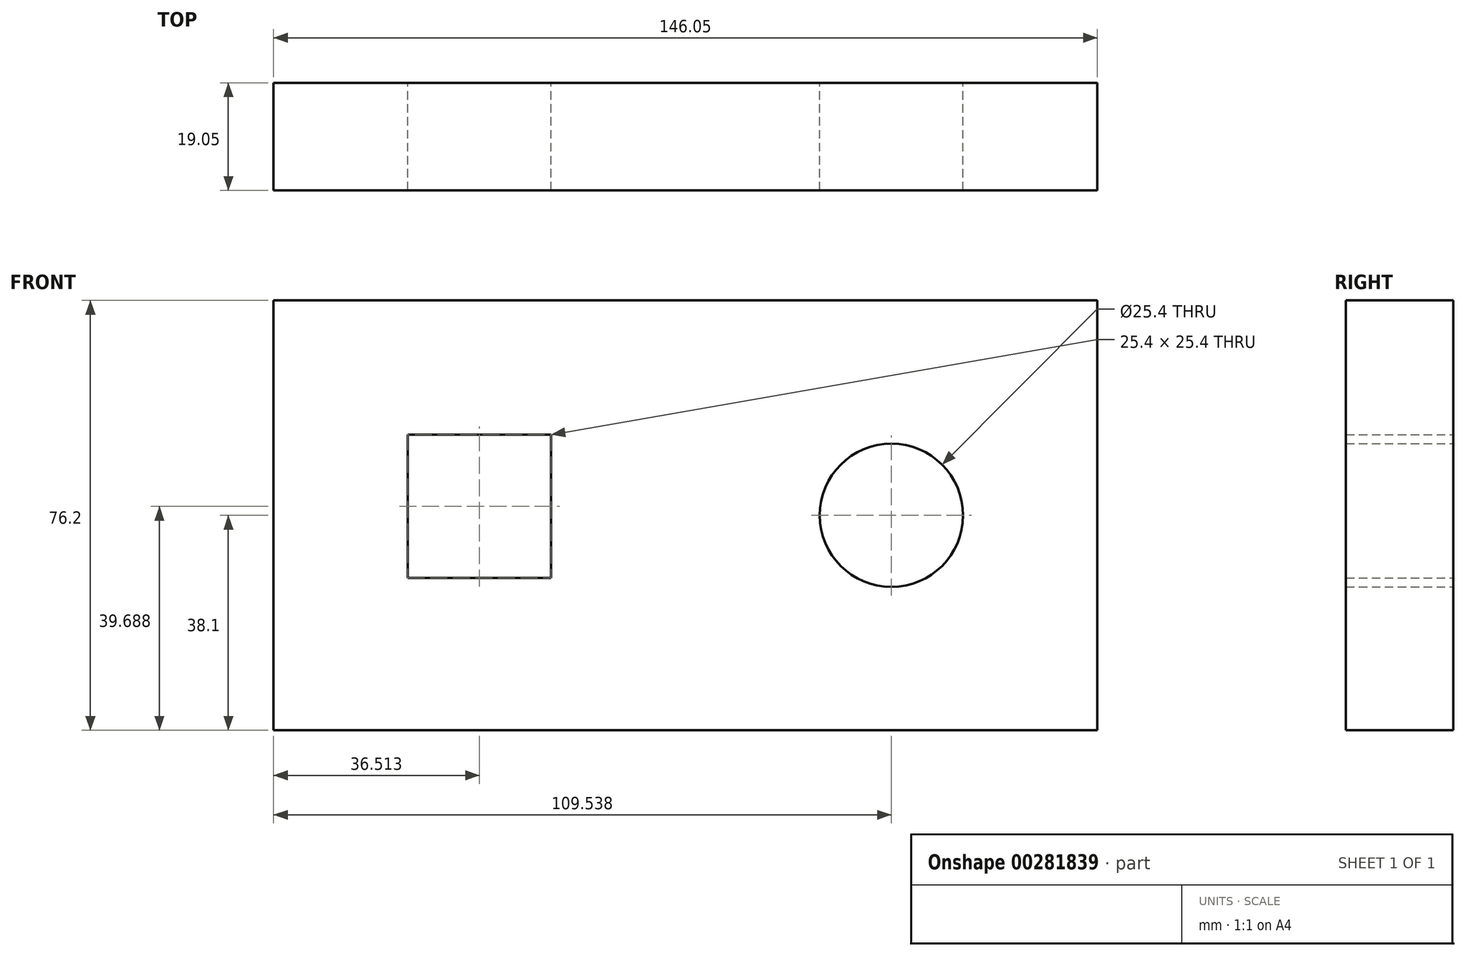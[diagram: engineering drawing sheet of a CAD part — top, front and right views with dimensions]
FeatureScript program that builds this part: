
annotation { "Feature Type Name" : "Feature", "Feature Type Description" : "" }
export const myFeature = defineFeature(function(context is Context, id is Id, definition is map)
    precondition{}
    {
        {
            var Q0;
            Q0=qCreatedBy(makeId("Front.planeOp"),FACE);
            var sketch = newSketch(context, id + "F0", { "sketchPlane" : qUnion([Q0])});
            skLineSegment(sketch, "E0.bottom", {"start": v(0, 0) * mm, "end": v(-146.05, 0) * mm});
            skLineSegment(sketch, "E0.top", {"start": v(0, 76.2) * mm, "end": v(-146.05, 76.2) * mm});
            skLineSegment(sketch, "E0.left", {"start": v(0, 0) * mm, "end": v(0, 76.2) * mm});
            skLineSegment(sketch, "E0.right", {"start": v(-146.05, 0) * mm, "end": v(-146.05, 76.2) * mm});
            skCircle(sketch, "E1", {"center": v(-36.51, 38.1) * mm, "radius": 12.7 * mm});
            skLineSegment(sketch, "E2.bottom", {"start": v(-122.24, 52.39) * mm, "end": v(-96.84, 52.39) * mm});
            skLineSegment(sketch, "E2.top", {"start": v(-122.24, 26.99) * mm, "end": v(-96.84, 26.99) * mm});
            skLineSegment(sketch, "E2.left", {"start": v(-122.24, 52.39) * mm, "end": v(-122.24, 26.99) * mm});
            skLineSegment(sketch, "E2.right", {"start": v(-96.84, 52.39) * mm, "end": v(-96.84, 26.99) * mm});
            skSolve(sketch);
        }
        {
            var Q0;
            Q0 = qSketchRegion(id + "F0", true);
            extrude(context, id + "F1", {"entities" : qUnion([Q0]), "depth" : 19.05 * mm});
        }
    });
